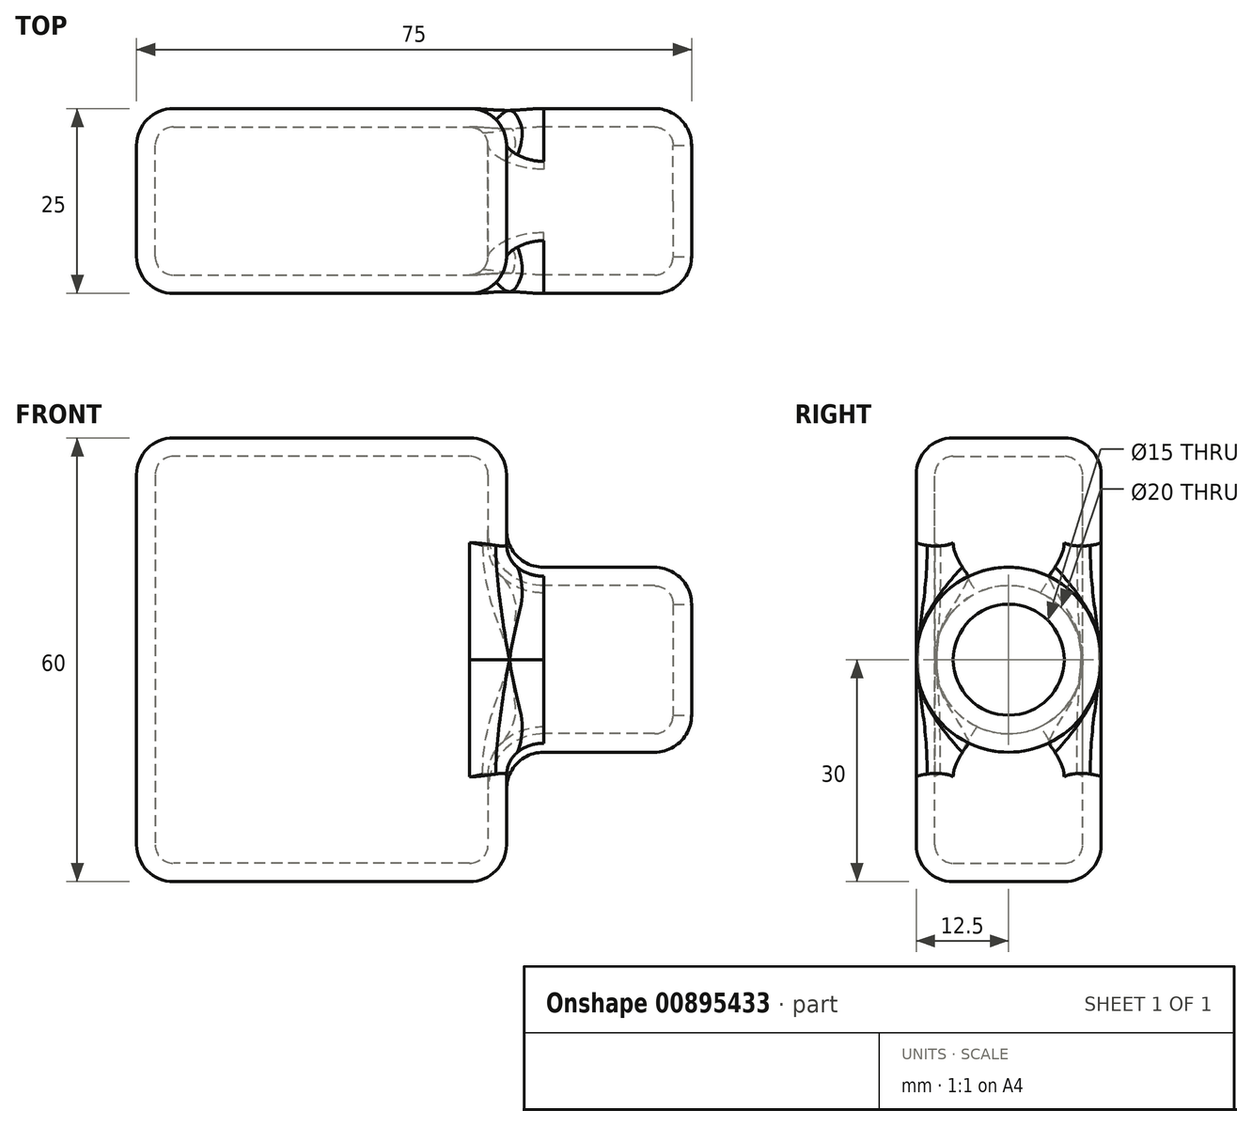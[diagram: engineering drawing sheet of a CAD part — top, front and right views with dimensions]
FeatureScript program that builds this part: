
annotation { "Feature Type Name" : "Feature", "Feature Type Description" : "" }
export const myFeature = defineFeature(function(context is Context, id is Id, definition is map)
    precondition{}
    {
        {
            var Q0;
            Q0=qCreatedBy(makeId("Front.planeOp"),FACE);
            var sketch = newSketch(context, id + "F0", { "sketchPlane" : qUnion([Q0])});
            skLineSegment(sketch, "E0.bottom", {"start": v(25, 30) * mm, "end": v(-25, 30) * mm});
            skLineSegment(sketch, "E0.top", {"start": v(25, -30) * mm, "end": v(-25, -30) * mm});
            skLineSegment(sketch, "E0.left", {"start": v(25, 30) * mm, "end": v(25, -30) * mm});
            skLineSegment(sketch, "E0.right", {"start": v(-25, 30) * mm, "end": v(-25, -30) * mm});
            skPoint(sketch, "E0.middle", {"position": v(0, 0) * mm});
            skSolve(sketch);
        }
        {
            var Q0;
            Q0 = qSketchRegion(id + "F0", true);
            extrude(context, id + "F1", {"entities" : qUnion([Q0]), "endBound" : BoundingType.SYMMETRIC, "depth" : 25 * mm, "offsetDistance" : 25 * mm});
        }
        {
            var Q0;
            Q0=makeQuery(id+"F1.opExtrude","SWEPT_FACE",FACE,{"disambiguationData":[OSD([sQuery(id+"F0.wireOp",EDGE,"E0.left")])]});
            var sketch = newSketch(context, id + "F2", { "sketchPlane" : qUnion([Q0])});
            skCircle(sketch, "E1", {"center": v(0, 0) * mm, "radius": 12.5 * mm});
            skSolve(sketch);
        }
        {
            var Q0;
            Q0 = qSketchRegion(id + "F2", true);
            extrude(context, id + "F3", {"entities" : qUnion([Q0]), "operationType" : NewBodyOperationType.ADD, "depth" : 25 * mm, "offsetDistance" : 25 * mm});
        }
        {
            var Q0;
            Q0=makeQuery(id+"F3.boolean.opBoolean","SPLIT",EDGE,{"disambiguationData":[OD(1.0)],"derivedFrom":makeQuery(id+"F3.opExtrude","CAP_EDGE",EDGE,{"disambiguationData":[OSD([sQuery(id+"F2.wireOp",EDGE,"E1")])],"isStart":true})});
            var Q1;
            Q1=makeQuery(id+"F1.opExtrude","CAP_FACE",FACE,{"disambiguationData":[OSD([sQuery(id+"F0.wireOp",EDGE,"E0.bottom"),sQuery(id+"F0.wireOp",EDGE,"E0.top"),sQuery(id+"F0.wireOp",EDGE,"E0.left"),sQuery(id+"F0.wireOp",EDGE,"E0.right")])],"isStart":false});
            var Q2;
            Q2=makeQuery(id+"F1.opExtrude","CAP_FACE",FACE,{"disambiguationData":[OSD([sQuery(id+"F0.wireOp",EDGE,"E0.bottom"),sQuery(id+"F0.wireOp",EDGE,"E0.top"),sQuery(id+"F0.wireOp",EDGE,"E0.left"),sQuery(id+"F0.wireOp",EDGE,"E0.right")])],"isStart":true});
            var Q3;
            Q3=makeQuery(id+"F3.opExtrude","CAP_FACE",FACE,{"disambiguationData":[OSD([sQuery(id+"F2.wireOp",EDGE,"E1")])],"isStart":false});
            var Q4;
            Q4=makeQuery(id+"F3.boolean.opBoolean","SPLIT",EDGE,{"disambiguationData":[OD(0.0)],"derivedFrom":makeQuery(id+"F3.opExtrude","CAP_EDGE",EDGE,{"disambiguationData":[OSD([sQuery(id+"F2.wireOp",EDGE,"E1")])],"isStart":true})});
            var Q5;
            Q5=makeQuery(id+"F1.opExtrude","SWEPT_EDGE",EDGE,{"disambiguationData":[OSD([sQuery(id+"F0.wireOp",EDGE,"E0.bottom"),sQuery(id+"F0.wireOp",EDGE,"E0.left")])]});
            var Q6;
            Q6=makeQuery(id+"F1.opExtrude","SWEPT_EDGE",EDGE,{"disambiguationData":[OSD([sQuery(id+"F0.wireOp",EDGE,"E0.bottom"),sQuery(id+"F0.wireOp",EDGE,"E0.right")])]});
            var Q7;
            Q7=makeQuery(id+"F1.opExtrude","SWEPT_EDGE",EDGE,{"disambiguationData":[OSD([sQuery(id+"F0.wireOp",EDGE,"E0.top"),sQuery(id+"F0.wireOp",EDGE,"E0.right")])]});
            var Q8;
            Q8=makeQuery(id+"F1.opExtrude","SWEPT_EDGE",EDGE,{"disambiguationData":[OSD([sQuery(id+"F0.wireOp",EDGE,"E0.top"),sQuery(id+"F0.wireOp",EDGE,"E0.left")])]});
            fillet(context, id + "F4", {"entities" : qUnion([Q0, Q1, Q2, Q3, Q4, Q5, Q6, Q7, Q8]), "radius" : 5 * mm, "tangentPropagation" : true, "allowEdgeOverflow" : false});
        }
        {
            var Q0;
            Q0=makeQuery(id+"F3.opExtrude","CAP_FACE",FACE,{"disambiguationData":[OSD([sQuery(id+"F2.wireOp",EDGE,"E1")])],"isStart":false});
            shell(context, id + "F5", {"entities" : qUnion([Q0]), "thickness" : 2.5 * mm});
        }
    });
